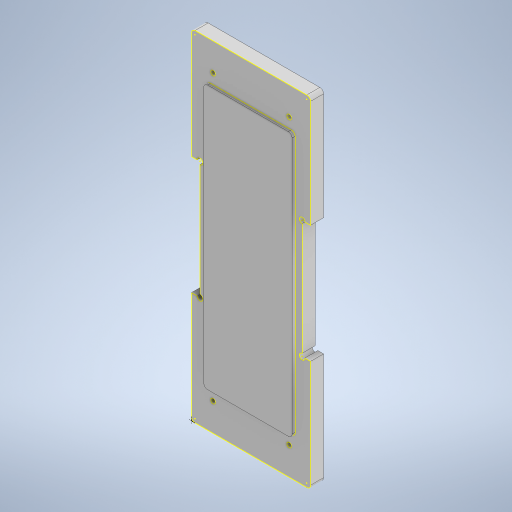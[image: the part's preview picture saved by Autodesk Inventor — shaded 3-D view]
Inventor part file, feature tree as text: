
AUTODESK INVENTOR PART (.ipt)
format: ipt  version: 2024.2 (Build 282272000, 272)  size: 1,384,448 bytes
history: native  units: mm
features: extrude x10, other x5, fillet x3, mirror x2, projected_geometry x2, surface_op x1, sketch x1
ambient origin geometry x8: Origin, YZ Plane, XZ Plane, XY Plane, X Axis, Y Axis, Z Axis, Center Point
bodies: Solid1 (feature_tree)
feature tree (24):
  extrude  "Extrusion1"  Depth=2.0mm
  extrude  "Extrusion2"  Depth=7.04mm TaperAngle=0.0deg
  extrude  "Extrusion3"  Depth=2.0mm
  extrude  "Extrusion4"  Depth=2.0mm
  fillet  "Fillet2"  Radius=1.6mm
  surface_op  "Sculpt1"
  extrude  "Extrusion5"  Depth=2.0mm
  extrude  "Extrusion6"  Depth=2.0mm
  extrude  "Extrusion7"  Depth=2.0mm
  extrude  "Extrusion8"  TaperAngle=0.0deg  [1 undecoded]
  fillet  "Fillet3"  Radius=142.1mm
  mirror  "Mirror1"
  extrude  "Extrusion9"  Depth=2.0mm
  mirror  "Mirror2"
  extrude  "Extrusion10"  Depth=10.0mm TaperAngle=0.0deg
  fillet  "Fillet4"  Radius=2.0mm
  sketch  "Sketch11"  dims[d0=67.0mm d1=186.0mm d2=7.04mm d3=0.0mm d4=48.0mm d5=142.6mm d6=1.6mm d7=0.0mm d9=2.5mm d10=41.0mm d11=153.0mm d12=0.0mm d13=0.0mm d14=142.1mm d16=47.5mm d17=10.0mm d18=0.0mm d19=2.0mm d20=0.0mm d22=0.0mm d23=4.0mm d24=0.0mm d25=0.0mm d26=0.05mm d27=0.5mm d28=0.0mm d30=10.0mm d31=0.0mm d32=4.0mm d33=4.0mm d34=4.0mm d35=10.0mm d36=0.0mm d37=2.0mm d38=2.0mm d39=0.0mm d40=0.0mm d41=1.75mm d42=6.0mm d43=63.5mm d44=3.0mm d45=3.0mm d46=0.0mm d47=0.0mm d49=0.0mm d50=0.0mm d51=2.0mm d52=64.12mm d53=183.0mm]
  projected_geometry  "Projected Loop1"
  projected_geometry  "Projected Loop2"
  other  "Composite1"
  other  "Srf1"
  other  "<userpath>\Google Drive\Unicorn 2020\CAD_V2\Manufacturing\PanelJigAssembly.iam"
  other  "PanelJigAssembly.iam"
  other  "1009799_3D:2"
note: 1 required parameter value undecoded (feature->parameter linkage not recoverable at this tier; creation-order binding heuristic only, values carry confidence <= 0.55)
